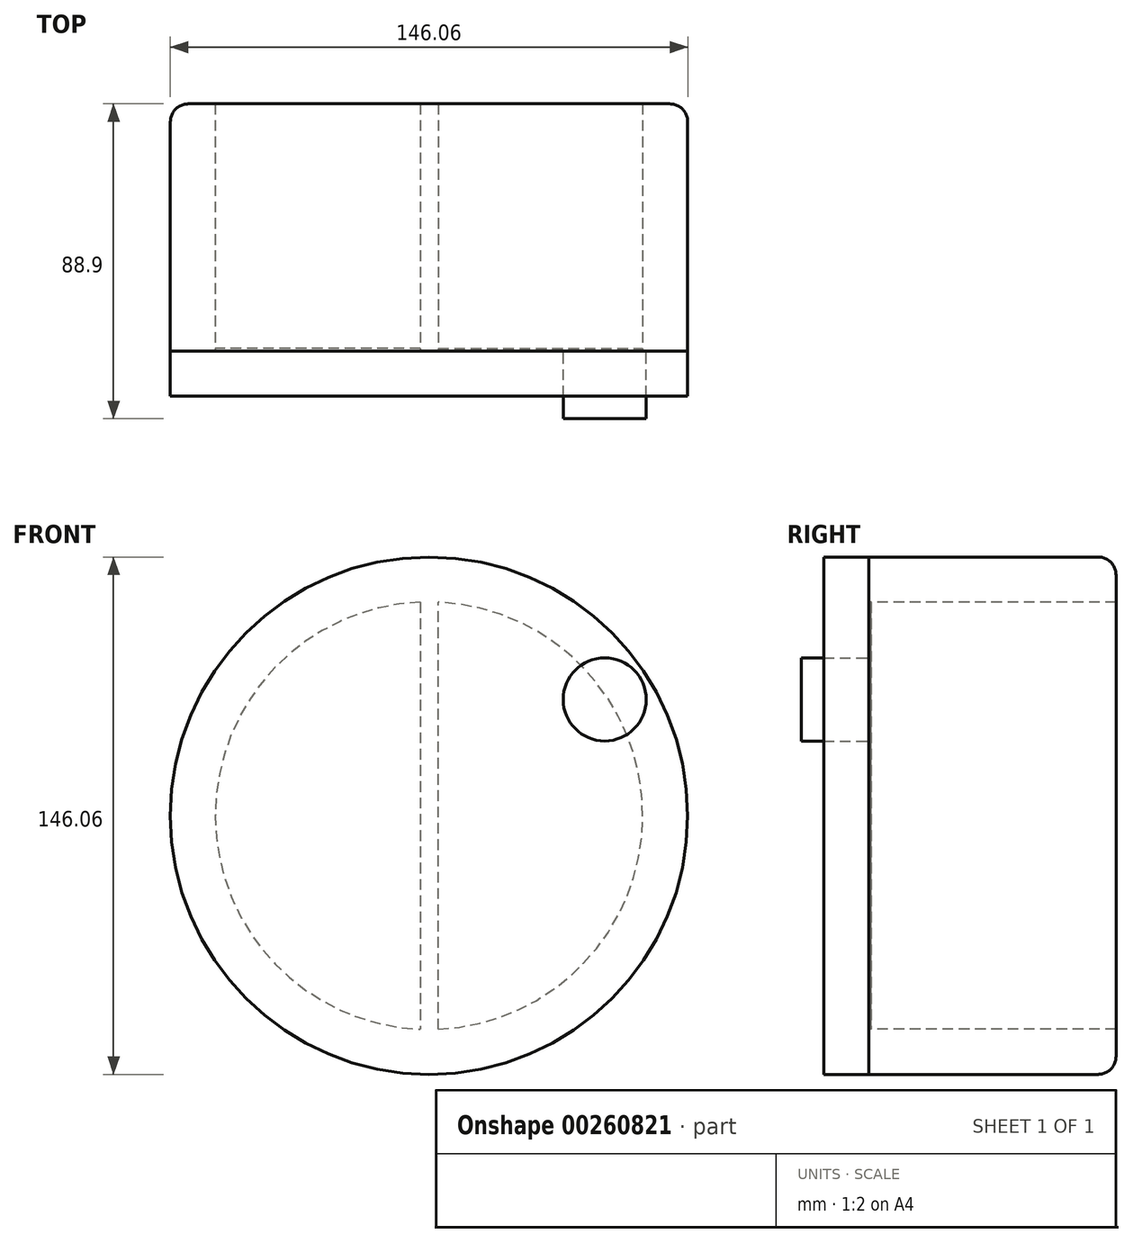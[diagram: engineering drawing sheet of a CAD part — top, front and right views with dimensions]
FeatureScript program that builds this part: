
annotation { "Feature Type Name" : "Feature", "Feature Type Description" : "" }
export const myFeature = defineFeature(function(context is Context, id is Id, definition is map)
    precondition{}
    {
        {
            var Q0;
            Q0=qCreatedBy(makeId("Front.planeOp"),FACE);
            var sketch = newSketch(context, id + "F0", { "sketchPlane" : qUnion([Q0])});
            skCircle(sketch, "E0", {"center": v(0, 0) * mm, "radius": 73.03 * mm});
            skCircle(sketch, "E1", {"center": v(0, 0) * mm, "radius": 60.33 * mm});
            skLineSegment(sketch, "E2", {"start": v(-2.42, 60.28) * mm, "end": v(-2.42, -60.28) * mm});
            skLineSegment(sketch, "E3", {"start": v(2.55, -60.27) * mm, "end": v(2.55, 60.27) * mm});
            skSolve(sketch);
        }
        {
            var Q0;
            Q0 = qSketchRegion(id + "F0", true);
            var Q1;
            {var subQ0=sQuery(id+"F0.wireOp",EDGE,"E2");Q1=makeQuery(id+"F0.imprint","IMPRINT",FACE,{"disambiguationData":[TD([[makeQuery(id+"F0.imprint","IMPRINT",EDGE,{"derivedFrom":subQ0}),1.0]])]});}
            extrude(context, id + "F1", {"entities" : qUnion([Q0, Q1]), "oppositeDirection" : true, "depth" : 69.85 * mm});
        }
        {
            var Q0;
            {var subQ0=sQuery(id+"F0.wireOp",EDGE,"E3");Q0=makeQuery(id+"F0.imprint","IMPRINT",FACE,{"disambiguationData":[TD([[makeQuery(id+"F0.imprint","IMPRINT",EDGE,{"derivedFrom":subQ0}),-1.0]])]});}
            var Q1;
            {var subQ0=sQuery(id+"F0.wireOp",EDGE,"E2");Q1=makeQuery(id+"F0.imprint","IMPRINT",FACE,{"disambiguationData":[TD([[makeQuery(id+"F0.imprint","IMPRINT",EDGE,{"derivedFrom":subQ0}),-1.0]])]});}
            extrude(context, id + "F2", {"entities" : qUnion([Q0, Q1]), "oppositeDirection" : true, "depth" : 0.76 * mm});
        }
        {
            var Q0;
            Q0=makeQuery(id+"F1.opExtrude","CAP_EDGE",EDGE,{"disambiguationData":[OSD([sQuery(id+"F0.wireOp",EDGE,"E0")])],"isStart":false});
            fillet(context, id + "F3", {"entities" : qUnion([Q0]), "radius" : 5.08 * mm, "tangentPropagation" : true, "allowEdgeOverflow" : false});
        }
        {
            var Q0;
            Q0=makeQuery(id+"F0.imprint","IMPRINT",FACE,{"disambiguationData":[TD([[makeQuery(id+"F0.imprint","IMPRINT",EDGE,{"derivedFrom":sQuery(id+"F0.wireOp",EDGE,"E0")}),1.0]])]});
            var Q1;
            {var subQ0=sQuery(id+"F0.wireOp",EDGE,"E2");Q1=makeQuery(id+"F0.imprint","IMPRINT",FACE,{"disambiguationData":[TD([[makeQuery(id+"F0.imprint","IMPRINT",EDGE,{"derivedFrom":subQ0}),-1.0]])]});}
            var Q2;
            {var subQ0=sQuery(id+"F0.wireOp",EDGE,"E2");Q2=makeQuery(id+"F0.imprint","IMPRINT",FACE,{"disambiguationData":[TD([[makeQuery(id+"F0.imprint","IMPRINT",EDGE,{"derivedFrom":subQ0}),1.0]])]});}
            var Q3;
            {var subQ0=sQuery(id+"F0.wireOp",EDGE,"E3");Q3=makeQuery(id+"F0.imprint","IMPRINT",FACE,{"disambiguationData":[TD([[makeQuery(id+"F0.imprint","IMPRINT",EDGE,{"derivedFrom":subQ0}),-1.0]])]});}
            extrude(context, id + "F4", {"entities" : qUnion([Q0, Q1, Q2, Q3]), "depth" : 12.7 * mm});
        }
        {
            var Q0;
            Q0=qCreatedBy(makeId("Front.planeOp"),FACE);
            var sketch = newSketch(context, id + "F5", { "sketchPlane" : qUnion([Q0])});
            skCircle(sketch, "E4", {"center": v(49.6, 32.82) * mm, "radius": 11.73 * mm});
            skSolve(sketch);
        }
        {
            var Q0;
            Q0 = qSketchRegion(id + "F5", true);
            extrude(context, id + "F6", {"entities" : qUnion([Q0]), "depth" : 19.05 * mm});
        }
    });
